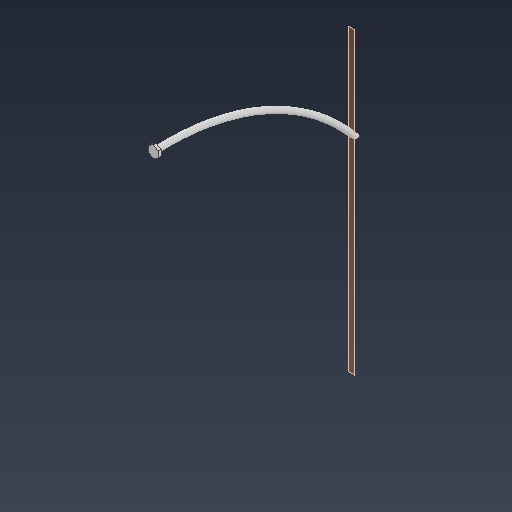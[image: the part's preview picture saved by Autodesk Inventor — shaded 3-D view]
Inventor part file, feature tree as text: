
AUTODESK INVENTOR PART (.ipt)
format: ipt  version: 2021 (Build 250183000, 183)  size: 231,424 bytes
history: native  units: mm
features: sketch x6, extrude x3, sweep x2, fillet x1, plane x1
ambient origin geometry x8: Origin, YZ Plane, XZ Plane, XY Plane, X Axis, Y Axis, Z Axis, Center Point
bodies: Solid1 (feature_tree)
feature tree (13):
  sketch  "Sketch1"  dims[d0=3300.0mm d1=1650.0mm]
  sweep  "Sweep1"
  sweep  "Sweep2"
  extrude  "Extrusion1"  Depth=30.0mm
  extrude  "Extrusion2"  Depth=1650.0mm
  fillet  "Fillet2"  [1 undecoded]
  plane  "Work Plane1"
  extrude  "Extrusion4"  Depth=3460.0mm
  sketch  "Sketch2"  dims[d2=0.0mm d3=40.0mm]
  sketch  "Sketch3"  dims[d4=0.0mm d5=0.0mm d6=30.0mm]
  sketch  "Sketch4"  dims[d7=0.0mm d8=1650.0mm d9=0.0mm d10=0.0mm]
  sketch  "Sketch5"  dims[d11=1810.0mm d12=3460.0mm]
  sketch  "Sketch6"  dims[d13=1730.0mm d14=1050.0mm d15=1730.0mm d16=1730.0mm d17=80.0mm d18=80.0mm d19=0.0mm d20=5.0mm d21=2.5mm d22=5.0mm d23=0.0mm d25=2.0mm d26=-1250.0mm d32=120.0deg d33=120.0deg d34=40.0mm d35=120.0deg d36=120.0deg d37=120.0deg d38=20.0mm d39=0.0mm]
note: 1 required parameter value undecoded (feature->parameter linkage not recoverable at this tier; creation-order binding heuristic only, values carry confidence <= 0.55)
